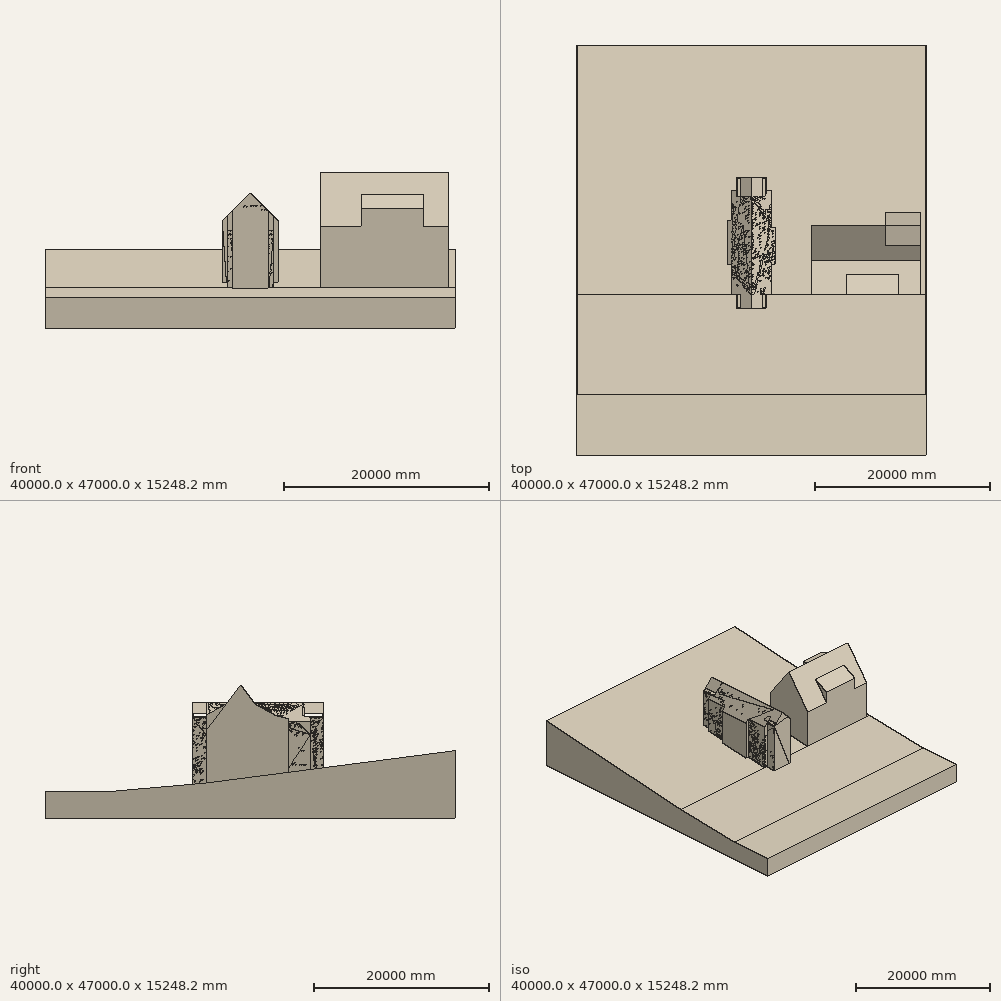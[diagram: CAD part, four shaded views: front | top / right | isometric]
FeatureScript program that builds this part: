
annotation { "Feature Type Name" : "Feature", "Feature Type Description" : "" }
export const myFeature = defineFeature(function(context is Context, id is Id, definition is map)
    precondition{}
    {
        {
            var Q0;
            Q0=qCreatedBy(makeId("Right.planeOp"),FACE);
            var sketch = newSketch(context, id + "F0", { "sketchPlane" : qUnion([Q0])});
            skLineSegment(sketch, "E0", {"start": v(0, 0) * mm, "end": v(11400, 1000) * mm});
            skLineSegment(sketch, "E1", {"start": v(11400, 1000) * mm, "end": v(23400, 2560) * mm});
            skLineSegment(sketch, "E2", {"start": v(23400, 2560) * mm, "end": v(40000, 4718) * mm});
            skLineSegment(sketch, "E3", {"start": v(0, 0) * mm, "end": v(-7000, 0) * mm});
            skLineSegment(sketch, "E4", {"start": v(-7000, 0) * mm, "end": v(-7000, -3000) * mm});
            skLineSegment(sketch, "E5", {"start": v(-7000, -3000) * mm, "end": v(40000, -3000) * mm});
            skLineSegment(sketch, "E6", {"start": v(40000, -3000) * mm, "end": v(40000, 4718) * mm});
            skSolve(sketch);
        }
        {
            var Q0;
            Q0=makeQuery(id+"F0.imprint","IMPRINT",FACE,{"disambiguationData":[TD([[makeQuery(id+"F0.imprint","IMPRINT",EDGE,{"derivedFrom":sQuery(id+"F0.wireOp",EDGE,"E0")}),-1.0]])]});
            extrude(context, id + "F1", {"entities" : qUnion([Q0]), "endBound" : BoundingType.SYMMETRIC, "depth" : 40000 * mm});
        }
        {
            var Q0;
            Q0=qCreatedBy(makeId("Top.planeOp"),FACE);
            var sketch = newSketch(context, id + "F2", { "sketchPlane" : qUnion([Q0])});
            skLineSegment(sketch, "E7.left", {"start": v(-2250, 11400) * mm, "end": v(-2250, 14900) * mm});
            skLineSegment(sketch, "E7.right", {"start": v(2250, 11400) * mm, "end": v(2250, 14900) * mm});
            skLineSegment(sketch, "E8", {"start": v(-2250, 14900) * mm, "end": v(-2750, 14900) * mm});
            skLineSegment(sketch, "E9", {"start": v(-2750, 14900) * mm, "end": v(-2750, 19900) * mm});
            skLineSegment(sketch, "E10", {"start": v(-2750, 19900) * mm, "end": v(-2250, 19900) * mm});
            skLineSegment(sketch, "E11", {"start": v(2250, 14900) * mm, "end": v(2750, 14900) * mm});
            skLineSegment(sketch, "E12", {"start": v(2750, 14900) * mm, "end": v(2750, 19100) * mm});
            skLineSegment(sketch, "E13", {"start": v(2750, 19100) * mm, "end": v(2250, 19100) * mm});
            skLineSegment(sketch, "E14", {"start": v(-2250, 23400) * mm, "end": v(-1750, 23400) * mm});
            skLineSegment(sketch, "E15", {"start": v(-1750, 23400) * mm, "end": v(-1750, 24900) * mm});
            skLineSegment(sketch, "E16", {"start": v(-1750, 24900) * mm, "end": v(1750, 24900) * mm});
            skLineSegment(sketch, "E17", {"start": v(1750, 24900) * mm, "end": v(1750, 23400) * mm});
            skLineSegment(sketch, "E18", {"start": v(1750, 23400) * mm, "end": v(2250, 23400) * mm});
            skLineSegment(sketch, "E19", {"start": v(-2250, 11400) * mm, "end": v(-1750, 11400) * mm});
            skLineSegment(sketch, "E20", {"start": v(-1750, 11400) * mm, "end": v(-1750, 9900) * mm});
            skLineSegment(sketch, "E21", {"start": v(-1750, 9900) * mm, "end": v(1750, 9900) * mm});
            skLineSegment(sketch, "E22", {"start": v(1750, 9900) * mm, "end": v(1750, 11400) * mm});
            skLineSegment(sketch, "E23", {"start": v(1750, 11400) * mm, "end": v(2250, 11400) * mm});
            skLineSegment(sketch, "E24.trimOffspring", {"start": v(-2250, 19900) * mm, "end": v(-2250, 23400) * mm});
            skLineSegment(sketch, "E25.trimOffspring", {"start": v(2250, 19100) * mm, "end": v(2250, 23400) * mm});
            skSolve(sketch);
        }
        {
            var Q0;
            Q0 = qSketchRegion(id + "F2", true);
            extrude(context, id + "F3", {"entities" : qUnion([Q0]), "depth" : 12530 * mm});
        }
        {
            var Q0;
            Q0=makeQuery(id+"F3.opExtrude","SWEPT_FACE",FACE,{"disambiguationData":[OSD([sQuery(id+"F2.wireOp",EDGE,"E12")])]});
            var sketch = newSketch(context, id + "F4", { "sketchPlane" : qUnion([Q0])});
            skLineSegment(sketch, "E26", {"start": v(17400, 12530) * mm, "end": v(9400, 4530) * mm});
            skLineSegment(sketch, "E27", {"start": v(9400, 4530) * mm, "end": v(9400, 13530) * mm});
            skLineSegment(sketch, "E28", {"start": v(9400, 13530) * mm, "end": v(25400, 13530) * mm});
            skLineSegment(sketch, "E29", {"start": v(25400, 13530) * mm, "end": v(25400, 4530) * mm});
            skLineSegment(sketch, "E30", {"start": v(25400, 4530) * mm, "end": v(17400, 12530) * mm});
            skSolve(sketch);
        }
        {
            var Q0;
            {var subQ1=sQuery(id+"F4.wireOp",EDGE,"E27");Q0=makeQuery(id+"F4.imprint","IMPRINT",FACE,{"disambiguationData":[TD([[makeQuery(id+"F4.imprint","IMPRINT",EDGE,{"derivedFrom":subQ1}),-1.0]])]});}
            var Q1;
            {var subQ0=sQuery(id+"F4.wireOp",EDGE,"E26");var subQ1=sQuery(id+"F2.wireOp",EDGE,"E12");var subQ2=makeQuery(id+"F3.opExtrude","CAP_EDGE",EDGE,{"disambiguationData":[OSD([subQ1])],"isStart":false});var subQ3=makeQuery(id+"F4.imprint","INTERSECT",VERTEX,{"derivedFrom":[subQ2,subQ0,sQuery(id+"F4.wireOp",EDGE,"E30")]});Q1=makeQuery(id+"F4.imprint","IMPRINT",FACE,{"disambiguationData":[TD([[makeQuery(id+"F4.imprint","IMPRINT",EDGE,{"disambiguationData":[TD([[subQ3,-1.0]])],"derivedFrom":subQ0}),-1.0]])]});}
            var Q2;
            {var subQ0=sQuery(id+"F4.wireOp",EDGE,"E30");var subQ1=sQuery(id+"F2.wireOp",EDGE,"E12");var subQ2=makeQuery(id+"F3.opExtrude","CAP_EDGE",EDGE,{"disambiguationData":[OSD([subQ1])],"isStart":false});var subQ3=makeQuery(id+"F4.imprint","INTERSECT",VERTEX,{"derivedFrom":[subQ2,sQuery(id+"F4.wireOp",EDGE,"E26"),subQ0]});Q2=makeQuery(id+"F4.imprint","IMPRINT",FACE,{"disambiguationData":[TD([[makeQuery(id+"F4.imprint","IMPRINT",EDGE,{"disambiguationData":[TD([[subQ3,1.0]])],"derivedFrom":subQ0}),-1.0]])]});}
            extrude(context, id + "F5", {"entities" : qUnion([Q0, Q1, Q2]), "operationType" : NewBodyOperationType.REMOVE, "oppositeDirection" : true, "depth" : 1000 * mm});
        }
        {
            var Q0;
            Q0=makeQuery(id+"F3.opExtrude","SWEPT_FACE",FACE,{"disambiguationData":[OSD([sQuery(id+"F2.wireOp",EDGE,"E9")])]});
            var sketch = newSketch(context, id + "F6", { "sketchPlane" : qUnion([Q0])});
            skLineSegment(sketch, "E31", {"start": v(-17400, 12530) * mm, "end": v(-25400, 4530) * mm});
            skLineSegment(sketch, "E32", {"start": v(-25400, 4530) * mm, "end": v(-25400, 13530) * mm});
            skLineSegment(sketch, "E33", {"start": v(-25400, 13530) * mm, "end": v(-9400, 13530) * mm});
            skLineSegment(sketch, "E34", {"start": v(-9400, 13530) * mm, "end": v(-9400, 4530) * mm});
            skLineSegment(sketch, "E35", {"start": v(-9400, 4530) * mm, "end": v(-17400, 12530) * mm});
            skSolve(sketch);
        }
        {
            var Q0;
            {var subQ1=sQuery(id+"F6.wireOp",EDGE,"E32");Q0=makeQuery(id+"F6.imprint","IMPRINT",FACE,{"disambiguationData":[TD([[makeQuery(id+"F6.imprint","IMPRINT",EDGE,{"derivedFrom":subQ1}),-1.0]])]});}
            var Q1;
            {var subQ0=sQuery(id+"F6.wireOp",EDGE,"E31");var subQ1=sQuery(id+"F2.wireOp",EDGE,"E9");var subQ2=makeQuery(id+"F3.opExtrude","CAP_EDGE",EDGE,{"disambiguationData":[OSD([subQ1])],"isStart":false});var subQ3=makeQuery(id+"F6.imprint","INTERSECT",VERTEX,{"derivedFrom":[subQ2,subQ0,sQuery(id+"F6.wireOp",EDGE,"E35")]});Q1=makeQuery(id+"F6.imprint","IMPRINT",FACE,{"disambiguationData":[TD([[makeQuery(id+"F6.imprint","IMPRINT",EDGE,{"disambiguationData":[TD([[subQ3,-1.0]])],"derivedFrom":subQ0}),-1.0]])]});}
            var Q2;
            {var subQ0=sQuery(id+"F6.wireOp",EDGE,"E35");var subQ1=sQuery(id+"F2.wireOp",EDGE,"E9");var subQ2=makeQuery(id+"F3.opExtrude","CAP_EDGE",EDGE,{"disambiguationData":[OSD([subQ1])],"isStart":false});var subQ3=makeQuery(id+"F6.imprint","INTERSECT",VERTEX,{"derivedFrom":[subQ2,sQuery(id+"F6.wireOp",EDGE,"E31"),subQ0]});Q2=makeQuery(id+"F6.imprint","IMPRINT",FACE,{"disambiguationData":[TD([[makeQuery(id+"F6.imprint","IMPRINT",EDGE,{"disambiguationData":[TD([[subQ3,1.0]])],"derivedFrom":subQ0}),-1.0]])]});}
            extrude(context, id + "F7", {"entities" : qUnion([Q0, Q1, Q2]), "operationType" : NewBodyOperationType.REMOVE, "oppositeDirection" : true, "depth" : 1000 * mm});
        }
        {
            var Q0;
            Q0=qCreatedBy(makeId("Right.planeOp"),FACE);
            var sketch = newSketch(context, id + "F8", { "sketchPlane" : qUnion([Q0])});
            skLineSegment(sketch, "E36", {"start": v(9400, 8980) * mm, "end": v(11400, 8980) * mm});
            skLineSegment(sketch, "E37", {"start": v(11400, 8980) * mm, "end": v(11400, 10340) * mm});
            skLineSegment(sketch, "E38.0", {"start": v(14900, 10030) * mm, "end": v(17400, 12530) * mm});
            skLineSegment(sketch, "E39.0", {"start": v(17400, 12530) * mm, "end": v(19900, 10030) * mm});
            skLineSegment(sketch, "E40", {"start": v(11400, 10340) * mm, "end": v(16230, 11360) * mm});
            skLineSegment(sketch, "E41", {"start": v(16230, 11360) * mm, "end": v(17400, 12530) * mm});
            skLineSegment(sketch, "E42", {"start": v(25400, 8980) * mm, "end": v(22700, 8980) * mm});
            skLineSegment(sketch, "E43", {"start": v(22700, 8980) * mm, "end": v(22700, 10340) * mm});
            skLineSegment(sketch, "E44", {"start": v(22700, 10340) * mm, "end": v(18570, 11360) * mm});
            skLineSegment(sketch, "E45", {"start": v(18570, 11360) * mm, "end": v(17400, 12530) * mm});
            skLineSegment(sketch, "E46", {"start": v(25400, 8980) * mm, "end": v(25400, 13480) * mm});
            skLineSegment(sketch, "E47", {"start": v(25400, 13480) * mm, "end": v(9400, 13480) * mm});
            skLineSegment(sketch, "E48", {"start": v(9400, 13480) * mm, "end": v(9400, 8980) * mm});
            skSolve(sketch);
        }
        {
            var Q0;
            Q0=makeQuery(id+"F8.imprint","IMPRINT",FACE,{"disambiguationData":[TD([[makeQuery(id+"F8.imprint","IMPRINT",EDGE,{"derivedFrom":sQuery(id+"F8.wireOp",EDGE,"E36")}),1.0]])]});
            extrude(context, id + "F9", {"entities" : qUnion([Q0]), "operationType" : NewBodyOperationType.REMOVE, "endBound" : BoundingType.SYMMETRIC, "oppositeDirection" : true, "depth" : 5000 * mm});
        }
        {
            var Q0;
            Q0=qCreatedBy(makeId("Right.planeOp"),FACE);
            cPlane(context, id + "F10", {"entities" : qUnion([Q0]), "cplaneType" : CPlaneType.OFFSET, "offset" : 6850 * mm, "width" : 150 * mm, "height" : 150 * mm});
        }
        {
            var Q0;
            Q0=qCreatedBy(id+"F10.planeOp",FACE);
            var sketch = newSketch(context, id + "F11", { "sketchPlane" : qUnion([Q0])});
            skLineSegment(sketch, "E49", {"start": v(11400, 0) * mm, "end": v(11400, 6940) * mm});
            skLineSegment(sketch, "E50", {"start": v(11400, 6940) * mm, "end": v(15400, 12248.18) * mm});
            skLineSegment(sketch, "E51", {"start": v(15400, 12248.18) * mm, "end": v(19400, 6940) * mm});
            skLineSegment(sketch, "E52", {"start": v(19400, 6940) * mm, "end": v(19400, 0) * mm});
            skLineSegment(sketch, "E53", {"start": v(19400, 0) * mm, "end": v(11400, 0) * mm});
            skSolve(sketch);
        }
        {
            var Q0;
            Q0=makeQuery(id+"F11.imprint","IMPRINT",FACE,{"disambiguationData":[TD([[makeQuery(id+"F11.imprint","IMPRINT",EDGE,{"derivedFrom":sQuery(id+"F11.wireOp",EDGE,"E49")}),-1.0]])]});
            extrude(context, id + "F12", {"entities" : qUnion([Q0]), "depth" : 12500 * mm});
        }
        {
            var Q0;
            Q0=qCreatedBy(id+"F10.planeOp",FACE);
            cPlane(context, id + "F13", {"entities" : qUnion([Q0]), "cplaneType" : CPlaneType.OFFSET, "offset" : 4000 * mm, "width" : 150 * mm, "height" : 150 * mm});
        }
        {
            var Q0;
            Q0=qCreatedBy(id+"F13.planeOp",FACE);
            var sketch = newSketch(context, id + "F14", { "sketchPlane" : qUnion([Q0])});
            skLineSegment(sketch, "E54", {"start": v(13740, 10050) * mm, "end": v(11400, 8750) * mm});
            skLineSegment(sketch, "E55", {"start": v(11400, 8750) * mm, "end": v(11400, 6940) * mm});
            skLineSegment(sketch, "E56", {"start": v(13740, 10050) * mm, "end": v(13740, 6940) * mm});
            skLineSegment(sketch, "E57", {"start": v(13740, 6940) * mm, "end": v(11400, 6940) * mm});
            skSolve(sketch);
        }
        {
            var Q0;
            Q0=makeQuery(id+"F14.imprint","IMPRINT",FACE,{"disambiguationData":[TD([[makeQuery(id+"F14.imprint","IMPRINT",EDGE,{"derivedFrom":sQuery(id+"F14.wireOp",EDGE,"E54")}),1.0]])]});
            extrude(context, id + "F15", {"entities" : qUnion([Q0]), "operationType" : NewBodyOperationType.ADD, "depth" : 6000 * mm});
        }
        {
            var Q0;
            Q0=makeQuery(id+"F12.opExtrude","CAP_FACE",FACE,{"disambiguationData":[OSD([sQuery(id+"F11.wireOp",EDGE,"E49"),sQuery(id+"F11.wireOp",EDGE,"E50"),sQuery(id+"F11.wireOp",EDGE,"E51"),sQuery(id+"F11.wireOp",EDGE,"E52"),sQuery(id+"F11.wireOp",EDGE,"E53")])],"isStart":false});
            var sketch = newSketch(context, id + "F16", { "sketchPlane" : qUnion([Q0])});
            skLineSegment(sketch, "E58", {"start": v(17060, 10045.28) * mm, "end": v(19400, 8750) * mm});
            skLineSegment(sketch, "E59", {"start": v(19400, 8750) * mm, "end": v(20900, 8360) * mm});
            skLineSegment(sketch, "E60", {"start": v(20900, 8360) * mm, "end": v(20900, 0) * mm});
            skLineSegment(sketch, "E61", {"start": v(20900, 0) * mm, "end": v(17060, 0) * mm});
            skLineSegment(sketch, "E62", {"start": v(17060, 0) * mm, "end": v(17060, 10045.28) * mm});
            skSolve(sketch);
        }
        {
            var Q0;
            {var subQ3=sQuery(id+"F16.wireOp",EDGE,"E58");Q0=makeQuery(id+"F16.imprint","IMPRINT",FACE,{"disambiguationData":[TD([[makeQuery(id+"F16.imprint","IMPRINT",EDGE,{"derivedFrom":subQ3}),-1.0]])]});}
            var Q1;
            {var subQ4=sQuery(id+"F11.wireOp",EDGE,"E52");var subQ7=makeQuery(id+"F12.opExtrude","CAP_EDGE",EDGE,{"disambiguationData":[OSD([subQ4])],"isStart":false});Q1=makeQuery(id+"F16.imprint","IMPRINT",FACE,{"disambiguationData":[TD([[makeQuery(id+"F16.imprint","IMPRINT",EDGE,{"derivedFrom":subQ7}),-1.0]])]});}
            extrude(context, id + "F17", {"entities" : qUnion([Q0, Q1]), "operationType" : NewBodyOperationType.ADD, "oppositeDirection" : true, "depth" : 4000 * mm});
        }
        {
            var Q0;
            Q0 = qSketchRegion(id + "F2", true);
            extrude(context, id + "F18", {"entities" : qUnion([Q0]), "depth" : 15000 * mm});
        }
        {
            var Q0;
            Q0=makeQuery(id+"F18.opExtrude","SWEPT_FACE",FACE,{"disambiguationData":[OSD([sQuery(id+"F2.wireOp",EDGE,"E21")])]});
            var sketch = newSketch(context, id + "F19", { "sketchPlane" : qUnion([Q0])});
            skLineSegment(sketch, "E63", {"start": v(0, 10280) * mm, "end": v(-3000, 7280) * mm});
            skLineSegment(sketch, "E64", {"start": v(-3000, 7280) * mm, "end": v(-3000, 15280) * mm});
            skLineSegment(sketch, "E65", {"start": v(-3000, 15280) * mm, "end": v(3000, 15280) * mm});
            skLineSegment(sketch, "E66", {"start": v(3000, 15280) * mm, "end": v(3000, 7280) * mm});
            skLineSegment(sketch, "E67", {"start": v(3000, 7280) * mm, "end": v(0, 10280) * mm});
            skSolve(sketch);
        }
        {
            var Q0;
            {var subQ0=sQuery(id+"F2.wireOp",EDGE,"E21");var subQ1=makeQuery(id+"F18.opExtrude","CAP_EDGE",EDGE,{"disambiguationData":[OSD([subQ0])],"isStart":false});Q0=makeQuery(id+"F19.imprint","IMPRINT",FACE,{"disambiguationData":[TD([[makeQuery(id+"F19.imprint","IMPRINT",EDGE,{"derivedFrom":subQ1}),-1.0]])]});}
            var Q1;
            {var subQ1=sQuery(id+"F19.wireOp",EDGE,"E64");Q1=makeQuery(id+"F19.imprint","IMPRINT",FACE,{"disambiguationData":[TD([[makeQuery(id+"F19.imprint","IMPRINT",EDGE,{"derivedFrom":subQ1}),-1.0]])]});}
            extrude(context, id + "F20", {"entities" : qUnion([Q0, Q1]), "operationType" : NewBodyOperationType.REMOVE, "oppositeDirection" : true, "depth" : 15000 * mm});
        }
        {
            var Q0;
            Q0=makeQuery(id+"F9.boolean.opBoolean","COPY",FACE,{"derivedFrom":makeQuery(id+"F9.opExtrude","SWEPT_FACE",FACE,{"disambiguationData":[OSD([sQuery(id+"F8.wireOp",EDGE,"E42")])]})});
            var sketch = newSketch(context, id + "F21", { "sketchPlane" : qUnion([Q0])});
            skLineSegment(sketch, "E68.bottom", {"start": v(-1650, 22700) * mm, "end": v(1650, 22700) * mm});
            skLineSegment(sketch, "E68.top", {"start": v(-1650, 24800) * mm, "end": v(1650, 24800) * mm});
            skLineSegment(sketch, "E68.left", {"start": v(-1650, 22700) * mm, "end": v(-1650, 24800) * mm});
            skLineSegment(sketch, "E68.right", {"start": v(1650, 22700) * mm, "end": v(1650, 24800) * mm});
            skLineSegment(sketch, "E69.bottom", {"start": v(-1650, 11400) * mm, "end": v(1650, 11400) * mm});
            skLineSegment(sketch, "E69.top", {"start": v(-1650, 10000) * mm, "end": v(1650, 10000) * mm});
            skLineSegment(sketch, "E69.left", {"start": v(-1650, 11400) * mm, "end": v(-1650, 10000) * mm});
            skLineSegment(sketch, "E69.right", {"start": v(1650, 11400) * mm, "end": v(1650, 10000) * mm});
            skSolve(sketch);
        }
        {
            var Q0;
            Q0 = qSketchRegion(id + "F21", true);
            extrude(context, id + "F22", {"entities" : qUnion([Q0]), "operationType" : NewBodyOperationType.REMOVE, "oppositeDirection" : true, "depth" : 1100 * mm});
        }
    });
